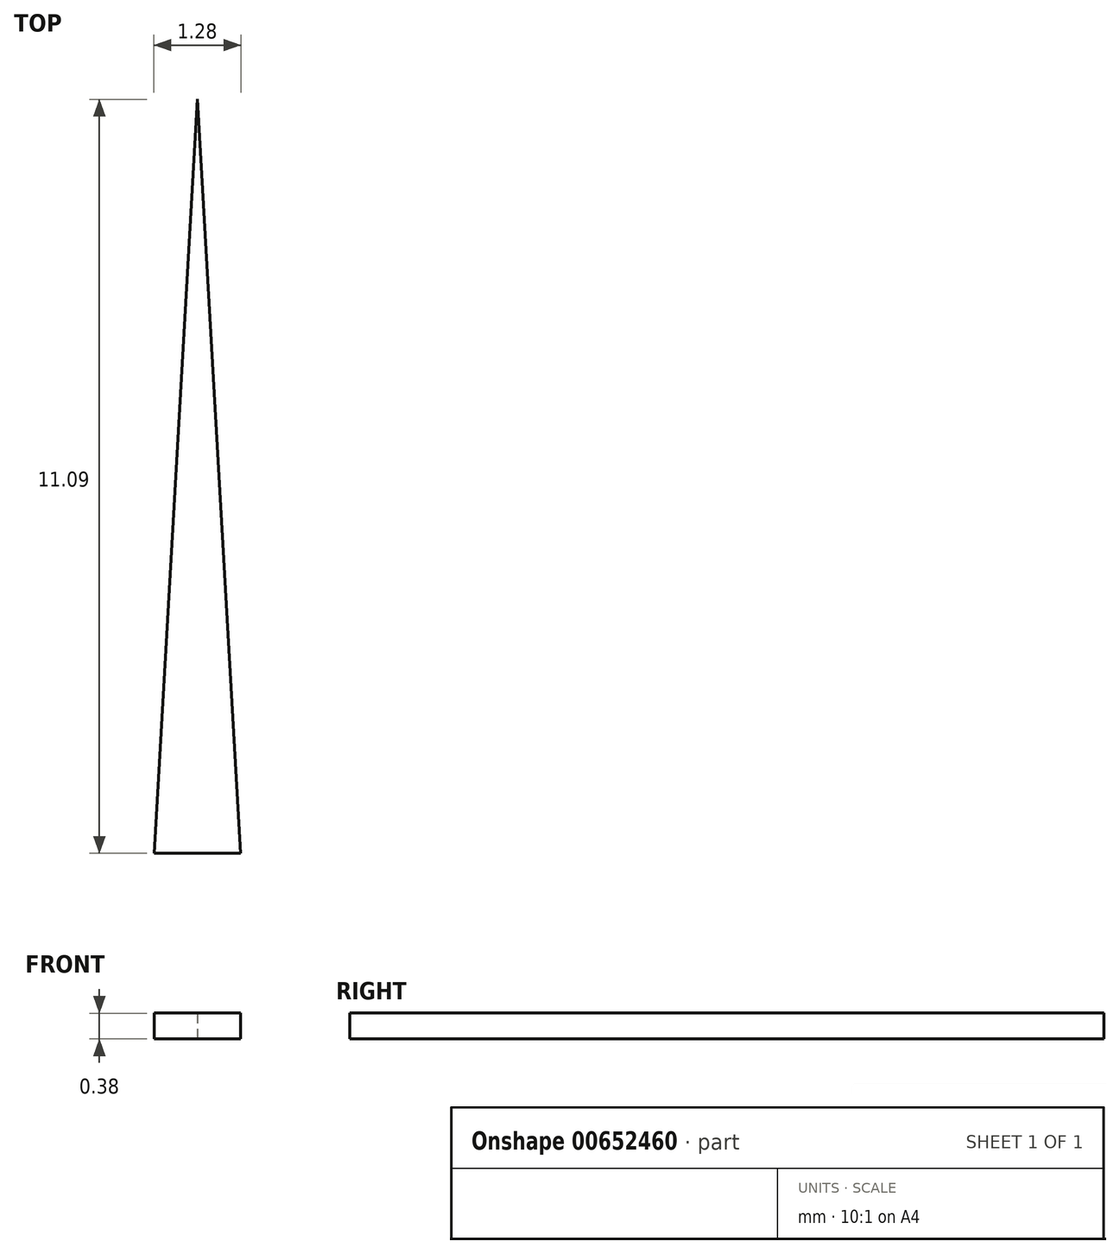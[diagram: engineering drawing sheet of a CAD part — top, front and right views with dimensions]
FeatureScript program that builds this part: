
annotation { "Feature Type Name" : "Feature", "Feature Type Description" : "" }
export const myFeature = defineFeature(function(context is Context, id is Id, definition is map)
    precondition{}
    {
        {
            var Q0;
            Q0=qCreatedBy(makeId("Top.planeOp"),FACE);
            var sketch = newSketch(context, id + "F0", { "sketchPlane" : qUnion([Q0])});
            skLineSegment(sketch, "E0", {"start": v(-0.63, 0) * mm, "end": v(0.63, 0) * mm});
            skLineSegment(sketch, "E1", {"start": v(0.63, 0) * mm, "end": v(0, 11.1) * mm});
            skLineSegment(sketch, "E2", {"start": v(0, 11.1) * mm, "end": v(-0.64, 0) * mm});
            skSolve(sketch);
        }
        {
            var Q0;
            Q0 = qSketchRegion(id + "F0", true);
            extrude(context, id + "F1", {"entities" : qUnion([Q0]), "depth" : 0.38 * mm, "offsetDistance" : 25.4 * mm});
        }
    });
